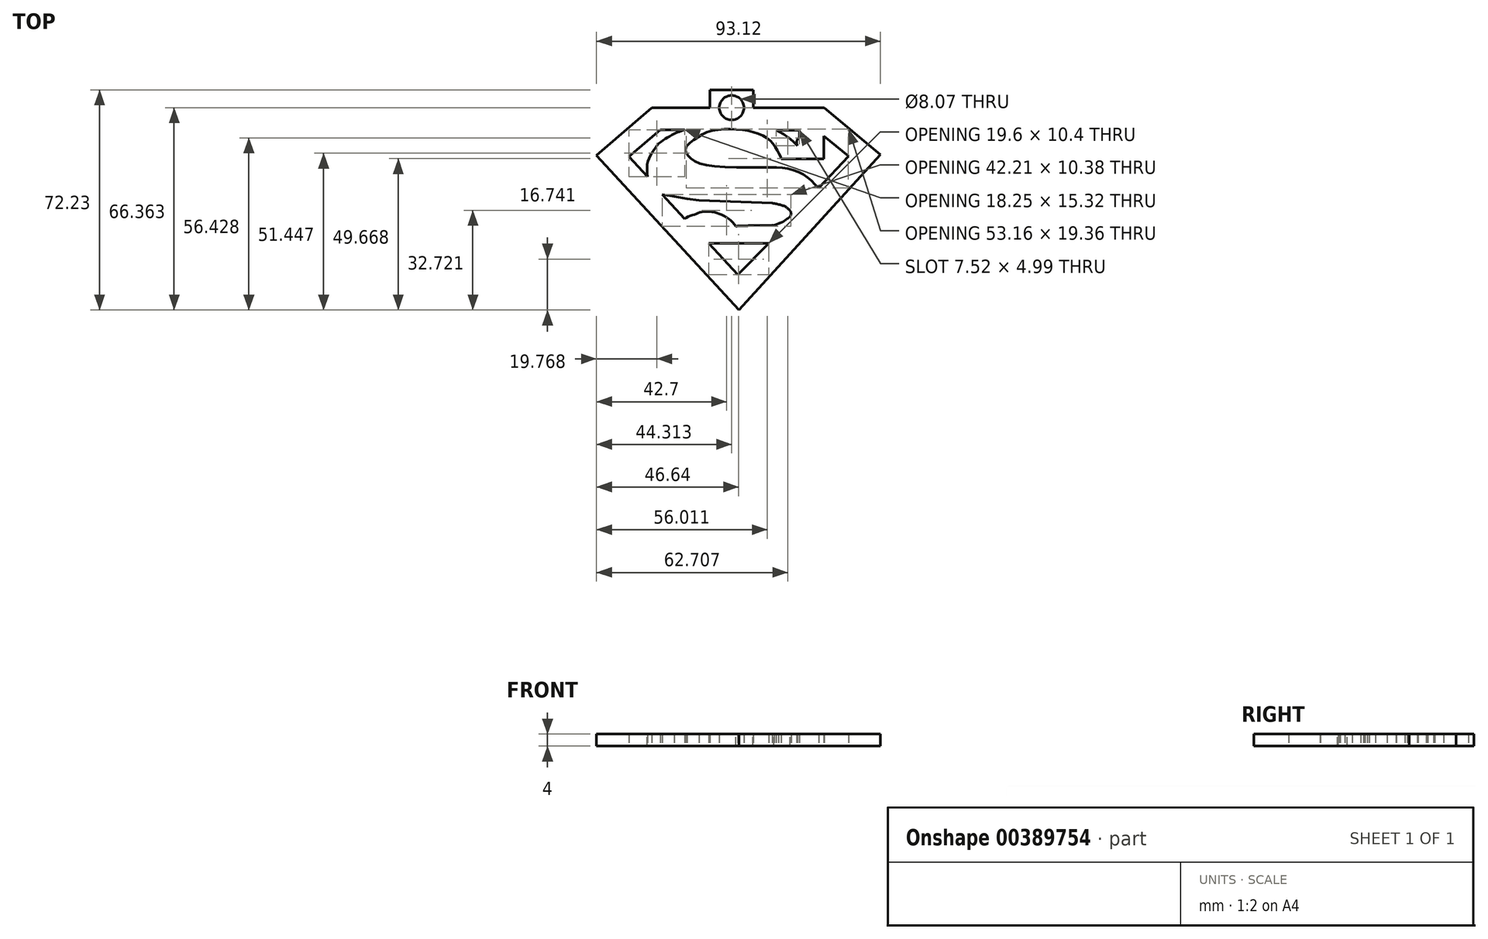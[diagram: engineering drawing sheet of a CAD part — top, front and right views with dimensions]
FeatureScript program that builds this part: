
annotation { "Feature Type Name" : "Feature", "Feature Type Description" : "" }
export const myFeature = defineFeature(function(context is Context, id is Id, definition is map)
    precondition{}
    {
        {
            var Q0;
            Q0=qCreatedBy(makeId("Top.planeOp"),FACE);
            var sketch = newSketch(context, id + "F0", { "sketchPlane" : qUnion([Q0])});
            skLineSegment(sketch, "E0", {"start": v(26.27, 26.5) * mm, "end": v(33.78, 26.5) * mm});
            skLineSegment(sketch, "E1", {"start": v(33.78, 26.5) * mm, "end": v(33.78, 24.2) * mm});
            skArc(sketch, "E2", {"start": v(33.18, 21.51) * mm, "mid": v(29.97, 24.35) * mm, "end": v(26.27, 26.5) * mm});
            skLineSegment(sketch, "E3", {"start": v(-15.98, 11.37) * mm, "end": v(-22.04, 17.98) * mm});
            skLineSegment(sketch, "E4", {"start": v(-22.04, 17.98) * mm, "end": v(-11.73, 26.69) * mm});
            skLineSegment(sketch, "E5", {"start": v(-11.73, 26.69) * mm, "end": v(-3.79, 26.69) * mm});
            skArc(sketch, "E6", {"start": v(33.78, 24.2) * mm, "mid": v(33.01, 22.96) * mm, "end": v(33.18, 21.51) * mm});
            skLineSegment(sketch, "E7", {"start": v(27.95, 17.12) * mm, "end": v(41.83, 17.12) * mm});
            skLineSegment(sketch, "E8", {"start": v(41.83, 17.12) * mm, "end": v(41.83, 24.7) * mm});
            skLineSegment(sketch, "E9", {"start": v(41.83, 24.7) * mm, "end": v(49.91, 18.01) * mm});
            skLineSegment(sketch, "E10", {"start": v(49.91, 18.01) * mm, "end": v(40.16, 7.57) * mm});
            skFitSpline(sketch, "E11", {"points": [v(-3.25, 21.22) * mm, v(3.43, 25.83) * mm, v(14.56, 26.72) * mm, v(22.99, 24.18) * mm, v(26.56, 20.1) * mm, v(27.95, 17.12) * mm], "startDerivative": vector(27.75, 25.2) * mm, "endDerivative": vector(8.58, -20.99) * mm});
            skLineSegment(sketch, "E12", {"start": v(-32.68, 18.28) * mm, "end": v(-14.57, 33.94) * mm});
            skLineSegment(sketch, "E13", {"start": v(-14.57, 33.94) * mm, "end": v(4.54, 33.94) * mm});
            skLineSegment(sketch, "E14", {"start": v(41.92, 33.94) * mm, "end": v(60.44, 18.53) * mm});
            skLineSegment(sketch, "E15", {"start": v(60.44, 18.53) * mm, "end": v(14.02, -32.42) * mm});
            skLineSegment(sketch, "E16", {"start": v(14.02, -32.42) * mm, "end": v(-32.68, 18.28) * mm});
            skLineSegment(sketch, "E17", {"start": v(4.16, -10.48) * mm, "end": v(13.68, -20.88) * mm});
            skLineSegment(sketch, "E18", {"start": v(13.68, -20.88) * mm, "end": v(23.76, -10.58) * mm});
            skLineSegment(sketch, "E19", {"start": v(23.76, -10.58) * mm, "end": v(4.16, -10.48) * mm});
            skLineSegment(sketch, "E20", {"start": v(-3.8, -2.47) * mm, "end": v(-11.08, 5.5) * mm});
            skPoint(sketch, "E21.1.internal.orphan", {"position": v(0, 3.55) * mm});
            skPoint(sketch, "E21.7.internal.orphan", {"position": v(30.95, 0) * mm});
            skLineSegment(sketch, "E22", {"start": v(-11.08, 5.5) * mm, "end": v(-7.15, 4.88) * mm});
            skLineSegment(sketch, "E23", {"start": v(-7.15, 4.88) * mm, "end": v(-2.92, 4.09) * mm});
            skLineSegment(sketch, "E24", {"start": v(-2.92, 4.09) * mm, "end": v(0.93, 3.55) * mm});
            skLineSegment(sketch, "E25", {"start": v(0.93, 3.55) * mm, "end": v(24.95, 2.67) * mm});
            skFitSpline(sketch, "E26", {"points": [v(24.95, 2.67) * mm, v(27.6, 2.08) * mm, v(29.38, 1.42) * mm, v(30.2, 0.75) * mm, v(30.95, 0) * mm, v(30.95, -1.5) * mm, v(29.63, -2.64) * mm, v(28.5, -3.43) * mm, v(26.93, -4.06) * mm, v(25.6, -4.6) * mm, v(24.95, -4.6) * mm, v(12.98, -4.9) * mm], "startDerivative": vector(25.82, -5.19) * mm, "endDerivative": vector(-71.25, -2.51) * mm});
            skFitSpline(sketch, "E27", {"points": [v(30.95, 0) * mm, v(30.95, -1.5) * mm, v(29.63, -2.64) * mm, v(28.5, -3.43) * mm, v(26.93, -4.06) * mm, v(25.6, -4.6) * mm, v(24.95, -4.6) * mm], "startDerivative": vector(1.9, -9.25) * mm, "endDerivative": vector(-5.35, 0.7) * mm});
            skLineSegment(sketch, "E28", {"start": v(24.95, -4.6) * mm, "end": v(18.25, -4.7) * mm});
            skFitSpline(sketch, "E29", {"points": [v(12.98, -4.9) * mm, v(11.2, -2.84) * mm, v(8.26, -1.13) * mm, v(5.77, -0.3) * mm, v(1.5, -0.34) * mm, v(0, -0.96) * mm, v(-1.97, -1.55) * mm, v(-3.8, -2.47) * mm], "startDerivative": vector(-10.54, 14.7) * mm, "endDerivative": vector(-13.78, -8.12) * mm});
            skFitSpline(sketch, "E30", {"points": [v(40.16, 7.57) * mm, v(37.26, 10.45) * mm, v(34.06, 12.58) * mm, v(29.58, 14.07) * mm, v(23.97, 14.32) * mm, v(6.14, 14.77) * mm, v(-0.5, 16.4) * mm, v(-2.58, 18.2) * mm, v(-3.41, 19.44) * mm, v(-3.25, 21.22) * mm], "startDerivative": vector(-27.64, 29.3) * mm, "endDerivative": vector(6.31, 28) * mm});
            skFitSpline(sketch, "E31", {"points": [v(-15.98, 11.37) * mm, v(-15.98, 15.6) * mm, v(-14.43, 19.18) * mm, v(-12.07, 22.34) * mm, v(-9.63, 24.03) * mm, v(-6.98, 25.5) * mm, v(-3.79, 26.69) * mm], "startDerivative": vector(-2.12, 24) * mm, "endDerivative": vector(20.2, 6.64) * mm});
            skLineSegment(sketch, "E32", {"start": v(18.25, -4.7) * mm, "end": v(12.98, -4.9) * mm});
            skLineSegment(sketch, "E33.top", {"start": v(4.54, 39.8) * mm, "end": v(18.72, 39.8) * mm});
            skLineSegment(sketch, "E33.left", {"start": v(4.54, 33.94) * mm, "end": v(4.54, 39.8) * mm});
            skLineSegment(sketch, "E33.right", {"start": v(18.72, 33.94) * mm, "end": v(18.72, 39.8) * mm});
            skCircle(sketch, "E34", {"center": v(11.63, 33.94) * mm, "radius": 4.03 * mm});
            skLineSegment(sketch, "E35.trimOffspring", {"start": v(18.72, 33.94) * mm, "end": v(41.92, 33.94) * mm});
            skSolve(sketch);
        }
        {
            var Q0;
            Q0=makeQuery(id+"F0.imprint","IMPRINT",FACE,{"disambiguationData":[TD([[makeQuery(id+"F0.imprint","IMPRINT",EDGE,{"derivedFrom":sQuery(id+"F0.wireOp",EDGE,"E0")}),1.0]])]});
            extrude(context, id + "F1", {"entities" : qUnion([Q0]), "depth" : 4 * mm, "offsetDistance" : 25 * mm});
        }
    });
